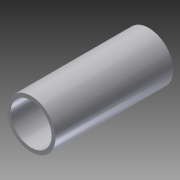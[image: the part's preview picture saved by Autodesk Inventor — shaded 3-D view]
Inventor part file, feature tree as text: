
AUTODESK INVENTOR PART (.ipt)
format: ipt  version: 2014 SP1 (Build 180222100, 222)  size: 84,480 bytes
history: native  units: in
note: dims shown in document units (in); Inventor stores cm internally (conversion verified against a paired STEP export)
features: extrude x1, sketch x1
ambient origin geometry x8: Origin, YZ Plane, XZ Plane, XY Plane, X Axis, Y Axis, Z Axis, Center Point
bodies: Solid1 (feature_tree)
feature tree (2):
  extrude  "Extrusion1"  Depth=5.75in
  sketch  "Sketch1"  dims[d0=2.0in d1=2.375in d2=5.75in d3=0.0in]
